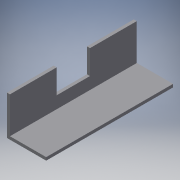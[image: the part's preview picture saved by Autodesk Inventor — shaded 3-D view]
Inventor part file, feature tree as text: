
AUTODESK INVENTOR PART (.ipt)
format: ipt  version: 2017 (Build 210142000, 142)  size: 111,104 bytes
history: native  units: in
note: dims shown in document units (in); Inventor stores cm internally (conversion verified against a paired STEP export)
features: extrude x3, sketch x3
ambient origin geometry x8: Origin, YZ Plane, XZ Plane, XY Plane, X Axis, Y Axis, Z Axis, Center Point
bodies: Solid1 (feature_tree)
feature tree (6):
  extrude  "Extrusion1"  Depth=1.625in
  extrude  "Extrusion2"  Depth=0.125in
  extrude  "Extrusion3"  Depth=1.0in
  sketch  "Sketch1"  dims[d0=5.25in d1=1.625in]
  sketch  "Sketch2"  dims[d2=0.125in d3=0.0in d4=0.125in]
  sketch  "Sketch3"  dims[d5=1.5in d6=0.0in d7=0.6875in d8=0.688in d9=1.0in d10=0.0in]
